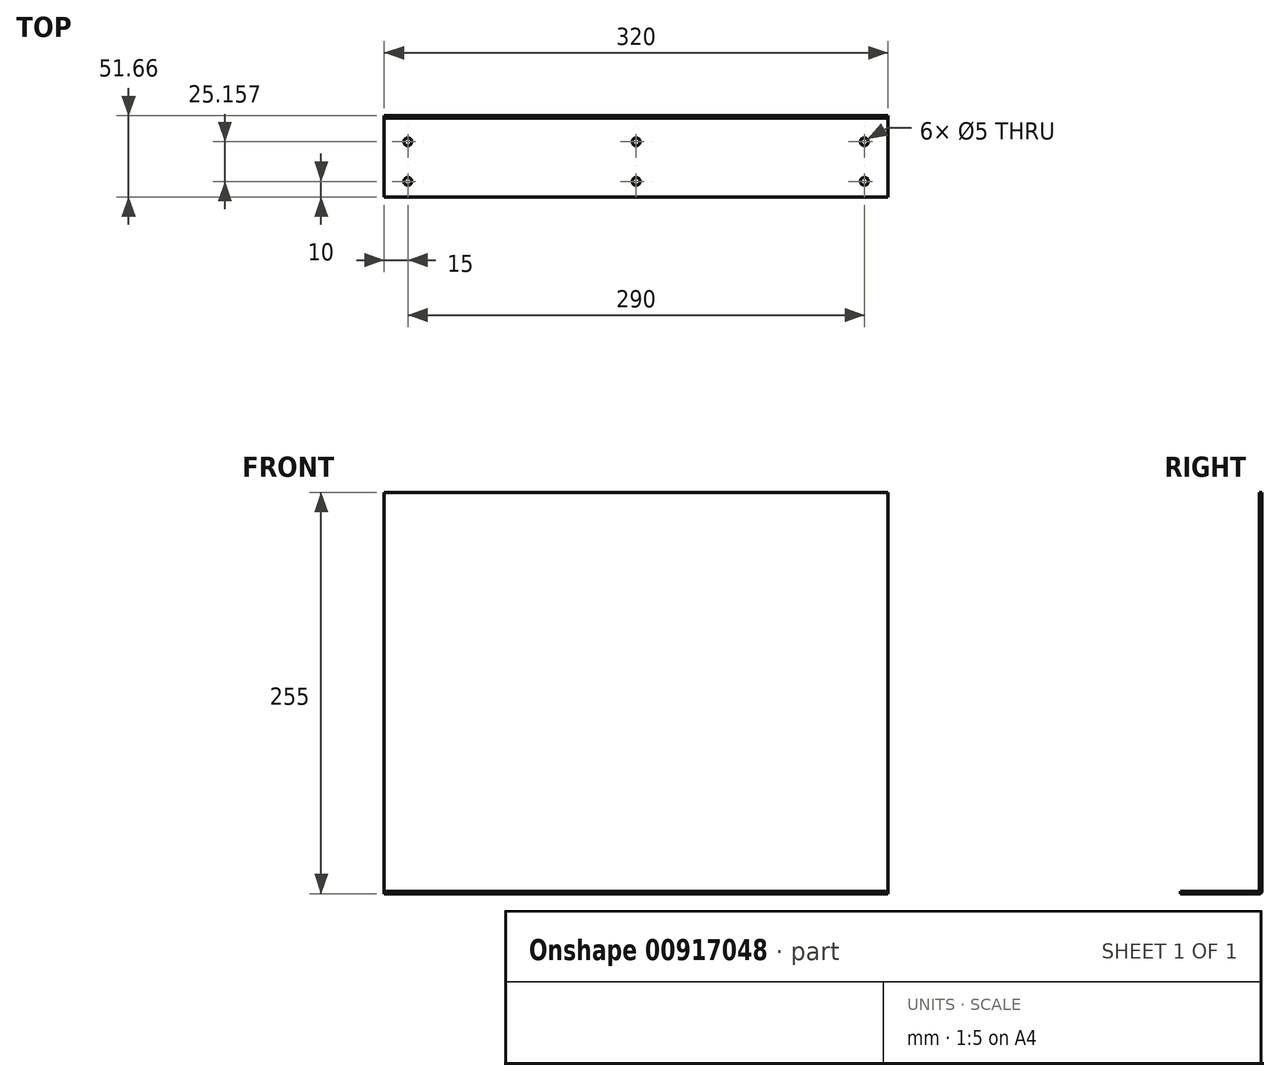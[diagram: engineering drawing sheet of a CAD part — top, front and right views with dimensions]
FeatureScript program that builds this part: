
annotation { "Feature Type Name" : "Feature", "Feature Type Description" : "" }
export const myFeature = defineFeature(function(context is Context, id is Id, definition is map)
    precondition{}
    {
        {
            var Q0;
            Q0=qCreatedBy(makeId("Right.planeOp"),FACE);
            var sketch = newSketch(context, id + "F0", { "sketchPlane" : qUnion([Q0])});
            skLineSegment(sketch, "E0", {"start": v(0, 0) * mm, "end": v(51.66, 0) * mm});
            skLineSegment(sketch, "E1", {"start": v(51.66, 0) * mm, "end": v(51.66, 255) * mm});
            skLineSegment(sketch, "E2", {"start": v(51.66, 255) * mm, "end": v(50.16, 255) * mm});
            skLineSegment(sketch, "E3", {"start": v(50.16, 255) * mm, "end": v(50.16, 1.5) * mm});
            skLineSegment(sketch, "E4", {"start": v(50.16, 1.5) * mm, "end": v(0, 1.5) * mm});
            skLineSegment(sketch, "E5", {"start": v(0, 1.5) * mm, "end": v(0, 0) * mm});
            skSolve(sketch);
        }
        {
            var Q0;
            Q0 = qSketchRegion(id + "F0", true);
            extrude(context, id + "F1", {"entities" : qUnion([Q0]), "depth" : 320 * mm, "offsetDistance" : 25 * mm});
        }
        {
            var Q0;
            Q0=makeQuery(id+"F1.opExtrude","SWEPT_EDGE",EDGE,{"disambiguationData":[OSD([sQuery(id+"F0.wireOp",EDGE,"E0"),sQuery(id+"F0.wireOp",EDGE,"E1")])]});
            fillet(context, id + "F2", {"entities" : qUnion([Q0]), "radius" : 1.5 * mm, "tangentPropagation" : true, "allowEdgeOverflow" : false});
        }
        {
            var Q0;
            Q0=makeQuery(id+"F1.opExtrude","SWEPT_EDGE",EDGE,{"disambiguationData":[OSD([sQuery(id+"F0.wireOp",EDGE,"E3"),sQuery(id+"F0.wireOp",EDGE,"E4")])]});
            fillet(context, id + "F3", {"entities" : qUnion([Q0]), "radius" : 0.5 * mm, "tangentPropagation" : true, "allowEdgeOverflow" : false});
        }
        {
            var Q0;
            Q0=makeQuery(id+"F1.opExtrude","SWEPT_FACE",FACE,{"disambiguationData":[OSD([sQuery(id+"F0.wireOp",EDGE,"E4")])]});
            var sketch = newSketch(context, id + "F4", { "sketchPlane" : qUnion([Q0])});
            skCircle(sketch, "E6", {"center": v(160, 10) * mm, "radius": 2.5 * mm});
            skPoint(sketch, "E6.centerSnap0", {"position": v(160, 0) * mm});
            skCircle(sketch, "E7", {"center": v(160, 35.16) * mm, "radius": 2.5 * mm});
            skCircle(sketch, "E8", {"center": v(15, 10) * mm, "radius": 2.5 * mm});
            skCircle(sketch, "E9", {"center": v(15, 35.16) * mm, "radius": 2.5 * mm});
            skCircle(sketch, "E10", {"center": v(305, 10) * mm, "radius": 2.5 * mm});
            skCircle(sketch, "E11", {"center": v(305, 35.16) * mm, "radius": 2.5 * mm});
            skSolve(sketch);
        }
        {
            var Q0;
            Q0=makeQuery(id+"F4.imprint","IMPRINT",FACE,{"disambiguationData":[TD([[makeQuery(id+"F4.imprint","IMPRINT",EDGE,{"derivedFrom":sQuery(id+"F4.wireOp",EDGE,"E9")}),1.0]])]});
            var Q1;
            Q1=makeQuery(id+"F4.imprint","IMPRINT",FACE,{"disambiguationData":[TD([[makeQuery(id+"F4.imprint","IMPRINT",EDGE,{"derivedFrom":sQuery(id+"F4.wireOp",EDGE,"E8")}),1.0]])]});
            var Q2;
            Q2=makeQuery(id+"F4.imprint","IMPRINT",FACE,{"disambiguationData":[TD([[makeQuery(id+"F4.imprint","IMPRINT",EDGE,{"derivedFrom":sQuery(id+"F4.wireOp",EDGE,"E6")}),1.0]])]});
            var Q3;
            Q3=makeQuery(id+"F4.imprint","IMPRINT",FACE,{"disambiguationData":[TD([[makeQuery(id+"F4.imprint","IMPRINT",EDGE,{"derivedFrom":sQuery(id+"F4.wireOp",EDGE,"E7")}),1.0]])]});
            var Q4;
            Q4=makeQuery(id+"F4.imprint","IMPRINT",FACE,{"disambiguationData":[TD([[makeQuery(id+"F4.imprint","IMPRINT",EDGE,{"derivedFrom":sQuery(id+"F4.wireOp",EDGE,"E11")}),1.0]])]});
            var Q5;
            Q5=makeQuery(id+"F4.imprint","IMPRINT",FACE,{"disambiguationData":[TD([[makeQuery(id+"F4.imprint","IMPRINT",EDGE,{"derivedFrom":sQuery(id+"F4.wireOp",EDGE,"E10")}),1.0]])]});
            extrude(context, id + "F5", {"entities" : qUnion([Q0, Q1, Q2, Q3, Q4, Q5]), "operationType" : NewBodyOperationType.REMOVE, "endBound" : BoundingType.THROUGH_ALL, "oppositeDirection" : true, "depth" : 25 * mm, "offsetDistance" : 25 * mm});
        }
    });
